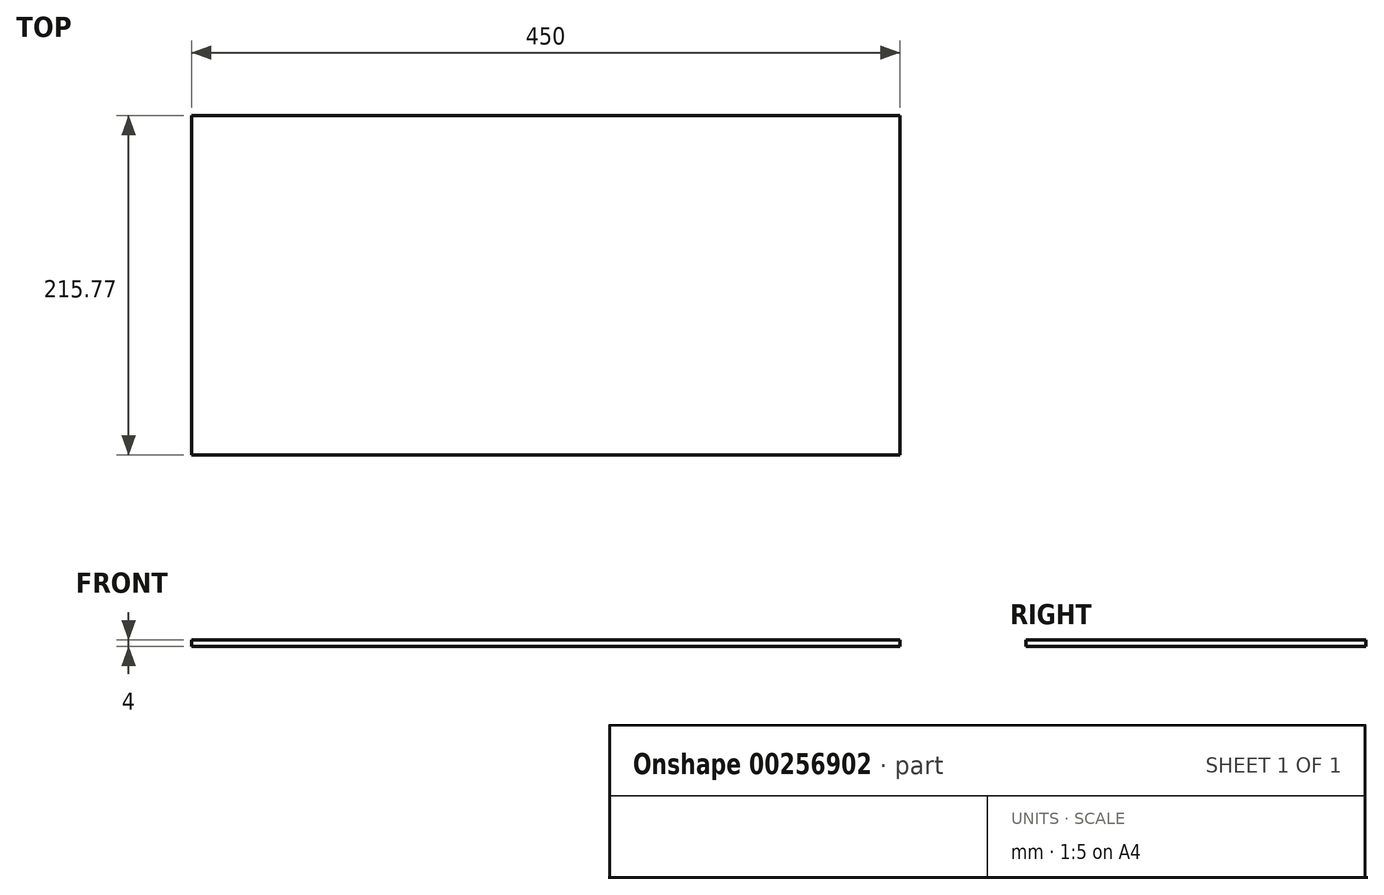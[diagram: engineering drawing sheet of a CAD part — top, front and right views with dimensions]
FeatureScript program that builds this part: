
annotation { "Feature Type Name" : "Feature", "Feature Type Description" : "" }
export const myFeature = defineFeature(function(context is Context, id is Id, definition is map)
    precondition{}
    {
        {
            var Q0;
            Q0=qCreatedBy(makeId("Top.planeOp"),FACE);
            var sketch = newSketch(context, id + "F0", { "sketchPlane" : qUnion([Q0])});
            skLineSegment(sketch, "E0.bottom", {"start": v(0, 0) * mm, "end": v(-450, 0) * mm});
            skLineSegment(sketch, "E0.top", {"start": v(0, 215.77) * mm, "end": v(-450, 215.77) * mm});
            skLineSegment(sketch, "E0.left", {"start": v(0, 0) * mm, "end": v(0, 215.77) * mm});
            skLineSegment(sketch, "E0.right", {"start": v(-450, 0) * mm, "end": v(-450, 215.77) * mm});
            skSolve(sketch);
        }
        {
            var Q0;
            Q0=makeQuery(id+"F0.imprint","IMPRINT",FACE,{"disambiguationData":[TD([[makeQuery(id+"F0.imprint","IMPRINT",EDGE,{"derivedFrom":sQuery(id+"F0.wireOp",EDGE,"E0.bottom")}),-1.0]])]});
            extrude(context, id + "F1", {"entities" : qUnion([Q0]), "depth" : 4 * mm});
        }
    });
